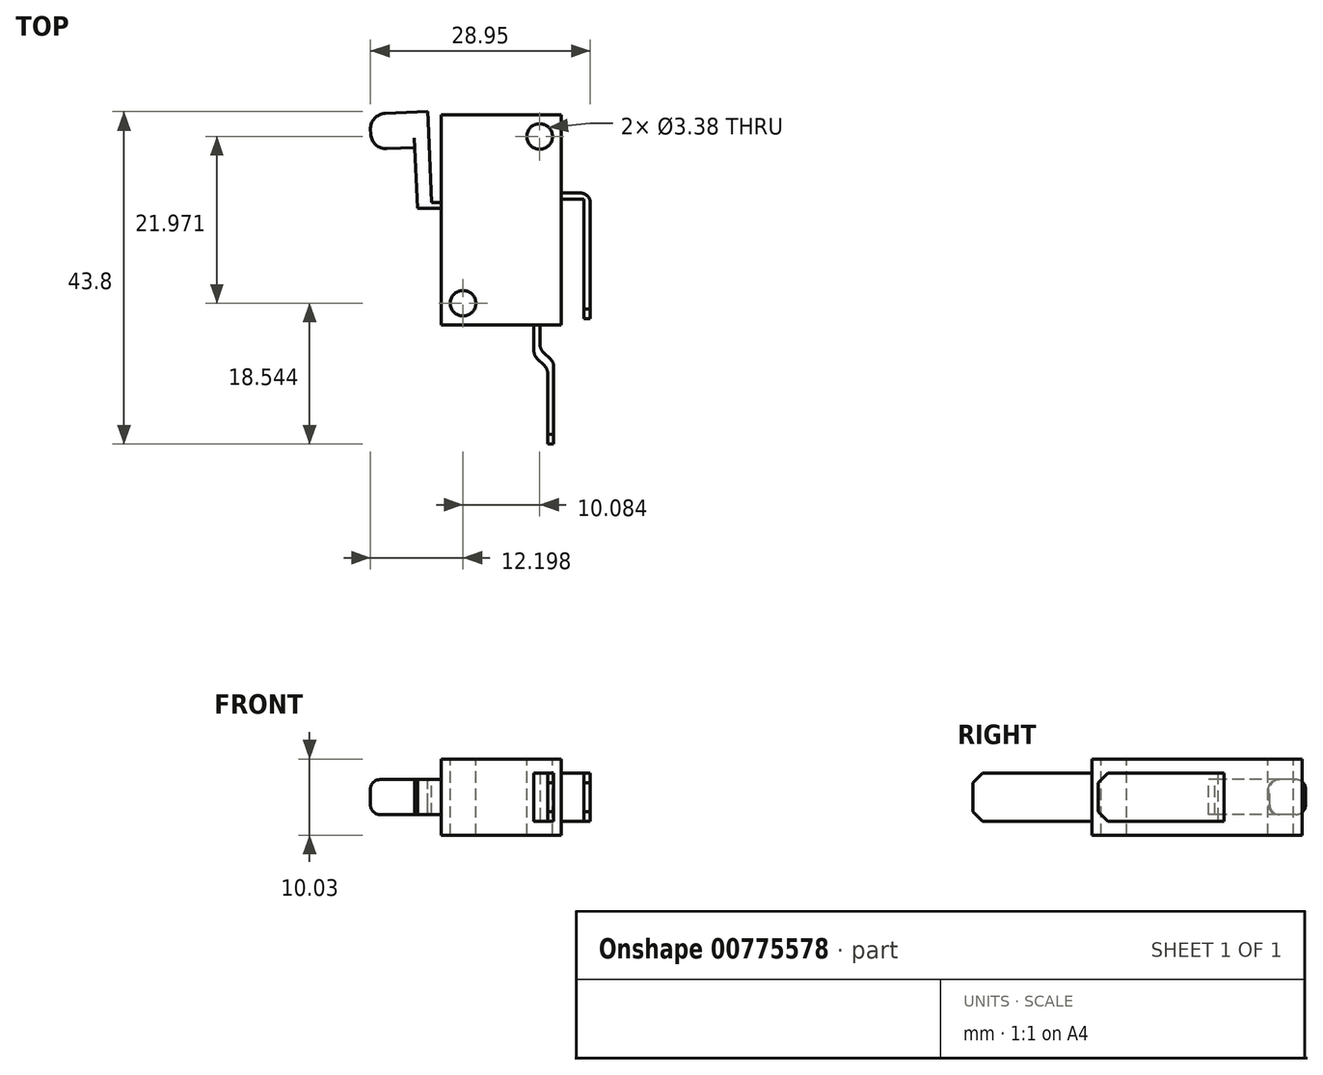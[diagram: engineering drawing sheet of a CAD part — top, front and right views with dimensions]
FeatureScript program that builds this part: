
annotation { "Feature Type Name" : "Feature", "Feature Type Description" : "" }
export const myFeature = defineFeature(function(context is Context, id is Id, definition is map)
    precondition{}
    {
        {
            var Q0;
            Q0=qCreatedBy(makeId("Top.planeOp"),FACE);
            var sketch = newSketch(context, id + "F0", { "sketchPlane" : qUnion([Q0])});
            skLineSegment(sketch, "E0.bottom", {"start": v(7.9, -13.84) * mm, "end": v(-7.9, -13.84) * mm});
            skLineSegment(sketch, "E0.top", {"start": v(7.9, 13.84) * mm, "end": v(-7.9, 13.84) * mm});
            skLineSegment(sketch, "E0.left", {"start": v(7.9, -13.84) * mm, "end": v(7.9, 13.84) * mm});
            skLineSegment(sketch, "E0.right", {"start": v(-7.9, -13.84) * mm, "end": v(-7.9, 13.84) * mm});
            skPoint(sketch, "E0.middle", {"position": v(0, 0) * mm});
            skSolve(sketch);
        }
        {
            var Q0;
            Q0 = qSketchRegion(id + "F0", true);
            extrude(context, id + "F1", {"entities" : qUnion([Q0]), "depth" : 10.03 * mm, "offsetDistance" : 25.4 * mm});
        }
        {
            var Q0;
            Q0=makeQuery(id+"F1.opExtrude","CAP_FACE",FACE,{"disambiguationData":[OSD([sQuery(id+"F0.wireOp",EDGE,"E0.bottom"),sQuery(id+"F0.wireOp",EDGE,"E0.top"),sQuery(id+"F0.wireOp",EDGE,"E0.left"),sQuery(id+"F0.wireOp",EDGE,"E0.right")])],"isStart":false});
            var sketch = newSketch(context, id + "F2", { "sketchPlane" : qUnion([Q0])});
            skCircle(sketch, "E1", {"center": v(5.04, 10.99) * mm, "radius": 1.69 * mm});
            skCircle(sketch, "E2", {"center": v(-5.04, -10.99) * mm, "radius": 1.69 * mm});
            skSolve(sketch);
        }
        {
            var Q0;
            Q0 = qSketchRegion(id + "F2", true);
            extrude(context, id + "F3", {"entities" : qUnion([Q0]), "operationType" : NewBodyOperationType.REMOVE, "endBound" : BoundingType.UP_TO_NEXT, "oppositeDirection" : true, "depth" : 25.4 * mm, "offsetDistance" : 25.4 * mm});
        }
        {
            var Q0;
            Q0=makeQuery(id+"F1.opExtrude","SWEPT_FACE",FACE,{"disambiguationData":[OSD([sQuery(id+"F0.wireOp",EDGE,"E0.left")])]});
            var sketch = newSketch(context, id + "F4", { "sketchPlane" : qUnion([Q0])});
            skLineSegment(sketch, "E3.bottom", {"start": v(3.53, 8.2) * mm, "end": v(2.72, 8.2) * mm});
            skLineSegment(sketch, "E3.top", {"start": v(3.53, 1.84) * mm, "end": v(2.72, 1.84) * mm});
            skLineSegment(sketch, "E3.left", {"start": v(3.53, 8.2) * mm, "end": v(3.53, 1.84) * mm});
            skLineSegment(sketch, "E3.right", {"start": v(2.72, 8.2) * mm, "end": v(2.72, 1.84) * mm});
            skLineSegment(sketch, "E4", {"start": v(13.84, 5.02) * mm, "end": v(-13.84, 5.02) * mm});
            skSolve(sketch);
        }
        {
            var Q0;
            Q0 = qSketchRegion(id + "F4", true);
            extrude(context, id + "F5", {"entities" : qUnion([Q0]), "operationType" : NewBodyOperationType.ADD, "depth" : 19.56 * mm - 15.75 * mm, "offsetDistance" : 25.4 * mm});
        }
        {
            var Q0;
            Q0=makeQuery(id+"F5.opExtrude","SWEPT_FACE",FACE,{"disambiguationData":[OSD([sQuery(id+"F4.wireOp",EDGE,"E3.right")])]});
            var sketch = newSketch(context, id + "F6", { "sketchPlane" : qUnion([Q0])});
            skLineSegment(sketch, "E5.bottom", {"start": v(11.7, 8.2) * mm, "end": v(10.9, 8.2) * mm});
            skLineSegment(sketch, "E5.top", {"start": v(11.7, 1.84) * mm, "end": v(10.9, 1.84) * mm});
            skLineSegment(sketch, "E5.left", {"start": v(11.7, 8.2) * mm, "end": v(11.7, 1.84) * mm});
            skLineSegment(sketch, "E5.right", {"start": v(10.9, 8.2) * mm, "end": v(10.9, 1.84) * mm});
            skSolve(sketch);
        }
        {
            var Q0;
            Q0 = qSketchRegion(id + "F6", true);
            extrude(context, id + "F7", {"entities" : qUnion([Q0]), "operationType" : NewBodyOperationType.ADD, "depth" : 15.75 * mm, "offsetDistance" : 25.4 * mm});
        }
        {
            var Q0;
            Q0=makeQuery(id+"F5.opExtrude","CAP_EDGE",EDGE,{"disambiguationData":[OSD([sQuery(id+"F4.wireOp",EDGE,"E3.left")])],"isStart":false});
            var Q1;
            Q1=makeQuery(id+"F7.opExtrude","CAP_EDGE",EDGE,{"disambiguationData":[OSD([sQuery(id+"F6.wireOp",EDGE,"E5.right")])],"isStart":true});
            fillet(context, id + "F8", {"entities" : qUnion([Q0, Q1]), "radius" : 1.27 * mm, "tangentPropagation" : true, "allowEdgeOverflow" : false});
        }
        {
            var Q0;
            Q0=makeQuery(id+"F7.opExtrude","CAP_EDGE",EDGE,{"disambiguationData":[OSD([sQuery(id+"F6.wireOp",EDGE,"E5.bottom")])],"isStart":false});
            var Q1;
            Q1=makeQuery(id+"F7.opExtrude","CAP_EDGE",EDGE,{"disambiguationData":[OSD([sQuery(id+"F6.wireOp",EDGE,"E5.top")])],"isStart":false});
            chamfer(context, id + "F9", {"entities" : qUnion([Q0, Q1]), "width" : 1.27 * mm, "tangentPropagation" : true});
        }
        {
            var Q0;
            Q0=makeQuery(id+"F1.opExtrude","SWEPT_FACE",FACE,{"disambiguationData":[OSD([sQuery(id+"F0.wireOp",EDGE,"E0.bottom")])]});
            var sketch = newSketch(context, id + "F10", { "sketchPlane" : qUnion([Q0])});
            skLineSegment(sketch, "E6.bottom", {"start": v(5.1, 8.2) * mm, "end": v(4.3, 8.2) * mm});
            skLineSegment(sketch, "E6.top", {"start": v(5.1, 1.84) * mm, "end": v(4.3, 1.84) * mm});
            skLineSegment(sketch, "E6.left", {"start": v(5.1, 8.2) * mm, "end": v(5.1, 1.84) * mm});
            skLineSegment(sketch, "E6.right", {"start": v(4.3, 8.2) * mm, "end": v(4.3, 1.84) * mm});
            skLineSegment(sketch, "E7", {"start": v(7.9, 5.02) * mm, "end": v(-7.9, 5.02) * mm});
            skSolve(sketch);
        }
        {
            var Q0;
            Q0 = qSketchRegion(id + "F10", true);
            extrude(context, id + "F11", {"entities" : qUnion([Q0]), "operationType" : NewBodyOperationType.ADD, "depth" : 3.17 * mm, "offsetDistance" : 25.4 * mm});
        }
        {
            var Q0;
            Q0=makeQuery(id+"F11.opExtrude","SWEPT_FACE",FACE,{"disambiguationData":[OSD([sQuery(id+"F10.wireOp",EDGE,"E6.bottom")])]});
            var sketch = newSketch(context, id + "F12", { "sketchPlane" : qUnion([Q0])});
            skLineSegment(sketch, "E8", {"start": v(5.1, -17.02) * mm, "end": v(4.3, -17.02) * mm});
            skLineSegment(sketch, "E9", {"start": v(4.3, -17.02) * mm, "end": v(4.3, -17.83) * mm});
            skLineSegment(sketch, "E10", {"start": v(4.3, -17.83) * mm, "end": v(5.1, -17.02) * mm});
            skSolve(sketch);
        }
        {
            var Q0;
            Q0 = qSketchRegion(id + "F12", true);
            var Q1;
            Q1=makeQuery(id+"F11.opExtrude","SWEPT_FACE",FACE,{"disambiguationData":[OSD([sQuery(id+"F10.wireOp",EDGE,"E6.top")])]});
            extrude(context, id + "F13", {"entities" : qUnion([Q0]), "operationType" : NewBodyOperationType.ADD, "endBound" : BoundingType.UP_TO_SURFACE, "oppositeDirection" : true, "depth" : 25.4 * mm, "endBoundEntityFace" : qUnion([Q1]), "offsetDistance" : 25.4 * mm});
        }
        {
            var Q0;
            Q0=makeQuery(id+"F13.opExtrude","SWEPT_FACE",FACE,{"disambiguationData":[OSD([sQuery(id+"F12.wireOp",EDGE,"E10")])]});
            var sketch = newSketch(context, id + "F14", { "sketchPlane" : qUnion([Q0])});
            skLineSegment(sketch, "E11.bottom", {"start": v(-8.42, 8.2) * mm, "end": v(-9.57, 8.2) * mm});
            skLineSegment(sketch, "E11.top", {"start": v(-8.42, 1.84) * mm, "end": v(-9.57, 1.84) * mm});
            skLineSegment(sketch, "E11.left", {"start": v(-8.42, 8.2) * mm, "end": v(-8.42, 1.84) * mm});
            skLineSegment(sketch, "E11.right", {"start": v(-9.57, 8.2) * mm, "end": v(-9.57, 1.84) * mm});
            skSolve(sketch);
        }
        {
            var Q0;
            Q0 = qSketchRegion(id + "F14", true);
            extrude(context, id + "F15", {"entities" : qUnion([Q0]), "operationType" : NewBodyOperationType.ADD, "depth" : 2.54 * mm, "offsetDistance" : 25.4 * mm});
        }
        {
            var Q0;
            Q0=makeQuery(id+"F15.boolean.opBoolean","MERGE",FACE,{"derivedFrom":[makeQuery(id+"F13.boolean.opBoolean","MERGE",FACE,{"derivedFrom":[makeQuery(id+"F11.opExtrude","SWEPT_FACE",FACE,{"disambiguationData":[OSD([sQuery(id+"F10.wireOp",EDGE,"E6.bottom")])]}),makeQuery(id+"F13.opExtrude","CAP_FACE",FACE,{"disambiguationData":[OSD([sQuery(id+"F12.wireOp",EDGE,"E8"),sQuery(id+"F12.wireOp",EDGE,"E9"),sQuery(id+"F12.wireOp",EDGE,"E10")])],"isStart":true})]}),makeQuery(id+"F15.opExtrude","SWEPT_FACE",FACE,{"disambiguationData":[OSD([sQuery(id+"F14.wireOp",EDGE,"E11.bottom")])]})]});
            var sketch = newSketch(context, id + "F16", { "sketchPlane" : qUnion([Q0])});
            skLineSegment(sketch, "E12", {"start": v(6.9, -18.81) * mm, "end": v(6.9, -19.63) * mm});
            skLineSegment(sketch, "E13", {"start": v(6.9, -19.63) * mm, "end": v(6.09, -19.63) * mm});
            skLineSegment(sketch, "E14", {"start": v(6.09, -19.63) * mm, "end": v(6.9, -18.81) * mm});
            skSolve(sketch);
        }
        {
            var Q0;
            Q0 = qSketchRegion(id + "F16", true);
            var Q1;
            {var subQ0=sQuery(id+"F10.wireOp",EDGE,"E6.top");Q1=makeQuery(id+"F15.boolean.opBoolean","MERGE",FACE,{"derivedFrom":[makeQuery(id+"F13.boolean.opBoolean","MERGE",FACE,{"derivedFrom":[makeQuery(id+"F11.opExtrude","SWEPT_FACE",FACE,{"disambiguationData":[OSD([subQ0])]}),makeQuery(id+"F13.opExtrude","CAP_FACE",FACE,{"disambiguationData":[OSD([subQ0])],"isStart":false})]}),makeQuery(id+"F15.opExtrude","SWEPT_FACE",FACE,{"disambiguationData":[OSD([sQuery(id+"F14.wireOp",EDGE,"E11.top")])]})]});}
            extrude(context, id + "F17", {"entities" : qUnion([Q0]), "operationType" : NewBodyOperationType.ADD, "endBound" : BoundingType.UP_TO_SURFACE, "oppositeDirection" : true, "depth" : 25.4 * mm, "endBoundEntityFace" : qUnion([Q1]), "offsetDistance" : 25.4 * mm});
        }
        {
            var Q0;
            Q0=makeQuery(id+"F17.opExtrude","SWEPT_FACE",FACE,{"disambiguationData":[OSD([sQuery(id+"F16.wireOp",EDGE,"E13")])]});
            var sketch = newSketch(context, id + "F18", { "sketchPlane" : qUnion([Q0])});
            skLineSegment(sketch, "E15.bottom", {"start": v(6.09, 8.2) * mm, "end": v(6.9, 8.2) * mm});
            skLineSegment(sketch, "E15.top", {"start": v(6.09, 1.84) * mm, "end": v(6.9, 1.84) * mm});
            skLineSegment(sketch, "E15.left", {"start": v(6.09, 8.2) * mm, "end": v(6.09, 1.84) * mm});
            skLineSegment(sketch, "E15.right", {"start": v(6.9, 8.2) * mm, "end": v(6.9, 1.84) * mm});
            skSolve(sketch);
        }
        {
            var Q0;
            Q0 = qSketchRegion(id + "F18", true);
            extrude(context, id + "F19", {"entities" : qUnion([Q0]), "operationType" : NewBodyOperationType.ADD, "depth" : 9.9 * mm, "offsetDistance" : 25.4 * mm});
        }
        {
            var Q0;
            Q0=makeQuery(id+"F15.boolean.opBoolean","MERGE",EDGE,{"derivedFrom":[makeQuery(id+"F13.opExtrude","SWEPT_EDGE",EDGE,{"disambiguationData":[OSD([sQuery(id+"F12.wireOp",EDGE,"E9"),sQuery(id+"F12.wireOp",EDGE,"E10")])]}),makeQuery(id+"F15.opExtrude","CAP_EDGE",EDGE,{"disambiguationData":[OSD([sQuery(id+"F14.wireOp",EDGE,"E11.right")])],"isStart":true})]});
            var Q1;
            {var subQ0=sQuery(id+"F10.wireOp",EDGE,"E6.left");Q1=makeQuery(id+"F15.boolean.opBoolean","MERGE",EDGE,{"derivedFrom":[makeQuery(id+"F13.boolean.opBoolean","MERGE",EDGE,{"derivedFrom":[makeQuery(id+"F11.opExtrude","CAP_EDGE",EDGE,{"disambiguationData":[OSD([subQ0])],"isStart":false}),makeQuery(id+"F13.opExtrude","SWEPT_EDGE",EDGE,{"disambiguationData":[OSD([sQuery(id+"F10.wireOp",EDGE,"E6.bottom"),subQ0,sQuery(id+"F12.wireOp",EDGE,"E8"),sQuery(id+"F12.wireOp",EDGE,"E10")])]})]}),makeQuery(id+"F15.opExtrude","CAP_EDGE",EDGE,{"disambiguationData":[OSD([sQuery(id+"F14.wireOp",EDGE,"E11.left")])],"isStart":true})]});}
            var Q2;
            {var subQ0=sQuery(id+"F14.wireOp",EDGE,"E11.left");Q2=makeQuery(id+"F17.boolean.opBoolean","MERGE",EDGE,{"derivedFrom":[makeQuery(id+"F15.opExtrude","CAP_EDGE",EDGE,{"disambiguationData":[OSD([subQ0])],"isStart":false}),makeQuery(id+"F17.opExtrude","SWEPT_EDGE",EDGE,{"disambiguationData":[OSD([sQuery(id+"F14.wireOp",EDGE,"E11.bottom"),subQ0,sQuery(id+"F16.wireOp",EDGE,"E12"),sQuery(id+"F16.wireOp",EDGE,"E14")])]})]});}
            var Q3;
            {var subQ0=sQuery(id+"F14.wireOp",EDGE,"E11.right");Q3=makeQuery(id+"F19.boolean.opBoolean","MERGE",EDGE,{"derivedFrom":[makeQuery(id+"F17.boolean.opBoolean","MERGE",EDGE,{"derivedFrom":[makeQuery(id+"F15.opExtrude","CAP_EDGE",EDGE,{"disambiguationData":[OSD([subQ0])],"isStart":false}),makeQuery(id+"F17.opExtrude","SWEPT_EDGE",EDGE,{"disambiguationData":[OSD([sQuery(id+"F14.wireOp",EDGE,"E11.bottom"),subQ0,sQuery(id+"F16.wireOp",EDGE,"E13"),sQuery(id+"F16.wireOp",EDGE,"E14")])]})]}),makeQuery(id+"F19.opExtrude","CAP_EDGE",EDGE,{"disambiguationData":[OSD([sQuery(id+"F18.wireOp",EDGE,"E15.left")])],"isStart":true})]});}
            fillet(context, id + "F20", {"entities" : qUnion([Q0, Q1, Q2, Q3]), "radius" : 1.27 * mm, "tangentPropagation" : true, "allowEdgeOverflow" : false});
        }
        {
            var Q0;
            Q0=makeQuery(id+"F19.opExtrude","CAP_EDGE",EDGE,{"disambiguationData":[OSD([sQuery(id+"F18.wireOp",EDGE,"E15.top")])],"isStart":false});
            var Q1;
            Q1=makeQuery(id+"F19.opExtrude","CAP_EDGE",EDGE,{"disambiguationData":[OSD([sQuery(id+"F18.wireOp",EDGE,"E15.bottom")])],"isStart":false});
            chamfer(context, id + "F21", {"entities" : qUnion([Q0, Q1]), "width" : 1.27 * mm, "tangentPropagation" : true});
        }
        {
            var Q0;
            Q0=makeQuery(id+"F1.opExtrude","SWEPT_FACE",FACE,{"disambiguationData":[OSD([sQuery(id+"F0.wireOp",EDGE,"E0.right")])]});
            var sketch = newSketch(context, id + "F22", { "sketchPlane" : qUnion([Q0])});
            skLineSegment(sketch, "E16.bottom", {"start": v(-2.31, 2.72) * mm, "end": v(-1.5, 2.72) * mm});
            skLineSegment(sketch, "E16.top", {"start": v(-2.31, 7.32) * mm, "end": v(-1.5, 7.32) * mm});
            skLineSegment(sketch, "E16.left", {"start": v(-2.31, 2.72) * mm, "end": v(-2.31, 7.32) * mm});
            skLineSegment(sketch, "E16.right", {"start": v(-1.5, 2.72) * mm, "end": v(-1.5, 7.32) * mm});
            skLineSegment(sketch, "E17", {"start": v(-13.84, 5.02) * mm, "end": v(13.84, 5.02) * mm});
            skSolve(sketch);
        }
        {
            var Q0;
            Q0 = qSketchRegion(id + "F22", true);
            extrude(context, id + "F23", {"entities" : qUnion([Q0]), "operationType" : NewBodyOperationType.ADD, "depth" : 1.27 * mm, "offsetDistance" : 25.4 * mm});
        }
        {
            var Q0;
            Q0=makeQuery(id+"F23.opExtrude","SWEPT_FACE",FACE,{"disambiguationData":[OSD([sQuery(id+"F22.wireOp",EDGE,"E16.top")])]});
            var sketch = newSketch(context, id + "F24", { "sketchPlane" : qUnion([Q0])});
            skLineSegment(sketch, "E18", {"start": v(-9.17, 1.58) * mm, "end": v(-9.17, 1.5) * mm});
            skLineSegment(sketch, "E19", {"start": v(-9.17, 1.5) * mm, "end": v(-11.06, 1.5) * mm});
            skLineSegment(sketch, "E20", {"start": v(-11.06, 1.5) * mm, "end": v(-9.17, 1.58) * mm});
            skSolve(sketch);
        }
        {
            var Q0;
            Q0 = qSketchRegion(id + "F24", true);
            var Q1;
            Q1=makeQuery(id+"F23.opExtrude","SWEPT_FACE",FACE,{"disambiguationData":[OSD([sQuery(id+"F22.wireOp",EDGE,"E16.bottom")])]});
            extrude(context, id + "F25", {"entities" : qUnion([Q0]), "operationType" : NewBodyOperationType.ADD, "endBound" : BoundingType.UP_TO_SURFACE, "oppositeDirection" : true, "depth" : 25.4 * mm, "endBoundEntityFace" : qUnion([Q1]), "offsetDistance" : 25.4 * mm});
        }
        {
            var Q0;
            Q0=makeQuery(id+"F25.opExtrude","SWEPT_FACE",FACE,{"disambiguationData":[OSD([sQuery(id+"F24.wireOp",EDGE,"E20")])]});
            var sketch = newSketch(context, id + "F26", { "sketchPlane" : qUnion([Q0])});
            skLineSegment(sketch, "E21.bottom", {"start": v(10.99, 2.72) * mm, "end": v(9.06, 2.72) * mm});
            skLineSegment(sketch, "E21.top", {"start": v(10.99, 7.32) * mm, "end": v(9.06, 7.32) * mm});
            skLineSegment(sketch, "E21.left", {"start": v(10.99, 2.72) * mm, "end": v(10.99, 7.32) * mm});
            skLineSegment(sketch, "E21.right", {"start": v(9.06, 2.72) * mm, "end": v(9.06, 7.32) * mm});
            skSolve(sketch);
        }
        {
            var Q0;
            Q0 = qSketchRegion(id + "F26", true);
            extrude(context, id + "F27", {"entities" : qUnion([Q0]), "operationType" : NewBodyOperationType.ADD, "depth" : 12.7 * mm, "offsetDistance" : 25.4 * mm});
        }
        {
            var Q0;
            Q0=makeQuery(id+"F27.opExtrude","SWEPT_FACE",FACE,{"disambiguationData":[OSD([sQuery(id+"F26.wireOp",EDGE,"E21.left")])]});
            var sketch = newSketch(context, id + "F28", { "sketchPlane" : qUnion([Q0])});
            skLineSegment(sketch, "E22.bottom", {"start": v(-14.68, 2.72) * mm, "end": v(-10.03, 2.72) * mm});
            skLineSegment(sketch, "E22.top", {"start": v(-14.68, 7.32) * mm, "end": v(-10.03, 7.32) * mm});
            skLineSegment(sketch, "E22.left", {"start": v(-14.68, 2.72) * mm, "end": v(-14.68, 7.32) * mm});
            skLineSegment(sketch, "E22.right", {"start": v(-10.03, 2.72) * mm, "end": v(-10.03, 7.32) * mm});
            skSolve(sketch);
        }
        {
            var Q0;
            Q0 = qSketchRegion(id + "F28", true);
            extrude(context, id + "F29", {"entities" : qUnion([Q0]), "operationType" : NewBodyOperationType.ADD, "depth" : 5.7 * mm, "offsetDistance" : 25.4 * mm});
        }
        {
            var Q0;
            Q0=makeQuery(id+"F29.opExtrude","CAP_EDGE",EDGE,{"disambiguationData":[OSD([sQuery(id+"F28.wireOp",EDGE,"E22.right")])],"isStart":false});
            var Q1;
            Q1=makeQuery(id+"F29.opExtrude","CAP_EDGE",EDGE,{"disambiguationData":[OSD([sQuery(id+"F28.wireOp",EDGE,"E22.left")])],"isStart":false});
            fillet(context, id + "F30", {"entities" : qUnion([Q0, Q1]), "radius" : 2.03 * mm, "tangentPropagation" : true, "allowEdgeOverflow" : false});
        }
        {
            var Q0;
            Q0=makeQuery(id+"F30.opFillet","BLEND_EDGE",EDGE,{"blendedFrom":[makeQuery(id+"F29.opExtrude","CAP_EDGE",EDGE,{"disambiguationData":[OSD([sQuery(id+"F28.wireOp",EDGE,"E22.left")])],"isStart":false}),makeQuery(id+"F29.boolean.opBoolean","MERGE",FACE,{"derivedFrom":[makeQuery(id+"F27.boolean.opBoolean","MERGE",FACE,{"derivedFrom":[makeQuery(id+"F25.boolean.opBoolean","MERGE",FACE,{"derivedFrom":[makeQuery(id+"F23.opExtrude","SWEPT_FACE",FACE,{"disambiguationData":[OSD([sQuery(id+"F22.wireOp",EDGE,"E16.top")])]}),makeQuery(id+"F25.opExtrude","CAP_FACE",FACE,{"disambiguationData":[OSD([sQuery(id+"F24.wireOp",EDGE,"E18"),sQuery(id+"F24.wireOp",EDGE,"E19"),sQuery(id+"F24.wireOp",EDGE,"E20")])],"isStart":true})]}),makeQuery(id+"F27.opExtrude","SWEPT_FACE",FACE,{"disambiguationData":[OSD([sQuery(id+"F26.wireOp",EDGE,"E21.top")])]})]}),makeQuery(id+"F29.opExtrude","SWEPT_FACE",FACE,{"disambiguationData":[OSD([sQuery(id+"F28.wireOp",EDGE,"E22.top")])]})]})],"blendedInto":[makeQuery(id+"F29.boolean.opBoolean","MERGE",FACE,{"derivedFrom":[makeQuery(id+"F27.boolean.opBoolean","MERGE",FACE,{"derivedFrom":[makeQuery(id+"F25.boolean.opBoolean","MERGE",FACE,{"derivedFrom":[makeQuery(id+"F23.opExtrude","SWEPT_FACE",FACE,{"disambiguationData":[OSD([sQuery(id+"F22.wireOp",EDGE,"E16.top")])]}),makeQuery(id+"F25.opExtrude","CAP_FACE",FACE,{"disambiguationData":[OSD([sQuery(id+"F24.wireOp",EDGE,"E18"),sQuery(id+"F24.wireOp",EDGE,"E19"),sQuery(id+"F24.wireOp",EDGE,"E20")])],"isStart":true})]}),makeQuery(id+"F27.opExtrude","SWEPT_FACE",FACE,{"disambiguationData":[OSD([sQuery(id+"F26.wireOp",EDGE,"E21.top")])]})]}),makeQuery(id+"F29.opExtrude","SWEPT_FACE",FACE,{"disambiguationData":[OSD([sQuery(id+"F28.wireOp",EDGE,"E22.top")])]})]})]});
            var Q1;
            Q1=makeQuery(id+"F30.opFillet","BLEND_EDGE",EDGE,{"blendedFrom":[makeQuery(id+"F29.opExtrude","CAP_EDGE",EDGE,{"disambiguationData":[OSD([sQuery(id+"F28.wireOp",EDGE,"E22.right")])],"isStart":false}),makeQuery(id+"F29.boolean.opBoolean","MERGE",FACE,{"derivedFrom":[makeQuery(id+"F27.boolean.opBoolean","MERGE",FACE,{"derivedFrom":[makeQuery(id+"F25.boolean.opBoolean","MERGE",FACE,{"derivedFrom":[makeQuery(id+"F23.opExtrude","SWEPT_FACE",FACE,{"disambiguationData":[OSD([sQuery(id+"F22.wireOp",EDGE,"E16.top")])]}),makeQuery(id+"F25.opExtrude","CAP_FACE",FACE,{"disambiguationData":[OSD([sQuery(id+"F24.wireOp",EDGE,"E18"),sQuery(id+"F24.wireOp",EDGE,"E19"),sQuery(id+"F24.wireOp",EDGE,"E20")])],"isStart":true})]}),makeQuery(id+"F27.opExtrude","SWEPT_FACE",FACE,{"disambiguationData":[OSD([sQuery(id+"F26.wireOp",EDGE,"E21.top")])]})]}),makeQuery(id+"F29.opExtrude","SWEPT_FACE",FACE,{"disambiguationData":[OSD([sQuery(id+"F28.wireOp",EDGE,"E22.top")])]})]})],"blendedInto":[makeQuery(id+"F29.boolean.opBoolean","MERGE",FACE,{"derivedFrom":[makeQuery(id+"F27.boolean.opBoolean","MERGE",FACE,{"derivedFrom":[makeQuery(id+"F25.boolean.opBoolean","MERGE",FACE,{"derivedFrom":[makeQuery(id+"F23.opExtrude","SWEPT_FACE",FACE,{"disambiguationData":[OSD([sQuery(id+"F22.wireOp",EDGE,"E16.top")])]}),makeQuery(id+"F25.opExtrude","CAP_FACE",FACE,{"disambiguationData":[OSD([sQuery(id+"F24.wireOp",EDGE,"E18"),sQuery(id+"F24.wireOp",EDGE,"E19"),sQuery(id+"F24.wireOp",EDGE,"E20")])],"isStart":true})]}),makeQuery(id+"F27.opExtrude","SWEPT_FACE",FACE,{"disambiguationData":[OSD([sQuery(id+"F26.wireOp",EDGE,"E21.top")])]})]}),makeQuery(id+"F29.opExtrude","SWEPT_FACE",FACE,{"disambiguationData":[OSD([sQuery(id+"F28.wireOp",EDGE,"E22.top")])]})]})]});
            var Q2;
            Q2=makeQuery(id+"F29.opExtrude","CAP_EDGE",EDGE,{"disambiguationData":[OSD([sQuery(id+"F28.wireOp",EDGE,"E22.top")])],"isStart":false});
            var Q3;
            Q3=makeQuery(id+"F29.opExtrude","CAP_EDGE",EDGE,{"disambiguationData":[OSD([sQuery(id+"F28.wireOp",EDGE,"E22.bottom")])],"isStart":false});
            var Q4;
            {var subQ0=sQuery(id+"F22.wireOp",EDGE,"E16.bottom");Q4=makeQuery(id+"F30.opFillet","BLEND_EDGE",EDGE,{"blendedFrom":[makeQuery(id+"F29.opExtrude","CAP_EDGE",EDGE,{"disambiguationData":[OSD([sQuery(id+"F28.wireOp",EDGE,"E22.right")])],"isStart":false}),makeQuery(id+"F29.boolean.opBoolean","MERGE",FACE,{"derivedFrom":[makeQuery(id+"F27.boolean.opBoolean","MERGE",FACE,{"derivedFrom":[makeQuery(id+"F25.boolean.opBoolean","MERGE",FACE,{"derivedFrom":[makeQuery(id+"F23.opExtrude","SWEPT_FACE",FACE,{"disambiguationData":[OSD([subQ0])]}),makeQuery(id+"F25.opExtrude","CAP_FACE",FACE,{"disambiguationData":[OSD([subQ0])],"isStart":false})]}),makeQuery(id+"F27.opExtrude","SWEPT_FACE",FACE,{"disambiguationData":[OSD([sQuery(id+"F26.wireOp",EDGE,"E21.bottom")])]})]}),makeQuery(id+"F29.opExtrude","SWEPT_FACE",FACE,{"disambiguationData":[OSD([sQuery(id+"F28.wireOp",EDGE,"E22.bottom")])]})]})],"blendedInto":[makeQuery(id+"F29.boolean.opBoolean","MERGE",FACE,{"derivedFrom":[makeQuery(id+"F27.boolean.opBoolean","MERGE",FACE,{"derivedFrom":[makeQuery(id+"F25.boolean.opBoolean","MERGE",FACE,{"derivedFrom":[makeQuery(id+"F23.opExtrude","SWEPT_FACE",FACE,{"disambiguationData":[OSD([subQ0])]}),makeQuery(id+"F25.opExtrude","CAP_FACE",FACE,{"disambiguationData":[OSD([subQ0])],"isStart":false})]}),makeQuery(id+"F27.opExtrude","SWEPT_FACE",FACE,{"disambiguationData":[OSD([sQuery(id+"F26.wireOp",EDGE,"E21.bottom")])]})]}),makeQuery(id+"F29.opExtrude","SWEPT_FACE",FACE,{"disambiguationData":[OSD([sQuery(id+"F28.wireOp",EDGE,"E22.bottom")])]})]})]});}
            var Q5;
            {var subQ0=sQuery(id+"F22.wireOp",EDGE,"E16.bottom");Q5=makeQuery(id+"F30.opFillet","BLEND_EDGE",EDGE,{"blendedFrom":[makeQuery(id+"F29.opExtrude","CAP_EDGE",EDGE,{"disambiguationData":[OSD([sQuery(id+"F28.wireOp",EDGE,"E22.left")])],"isStart":false}),makeQuery(id+"F29.boolean.opBoolean","MERGE",FACE,{"derivedFrom":[makeQuery(id+"F27.boolean.opBoolean","MERGE",FACE,{"derivedFrom":[makeQuery(id+"F25.boolean.opBoolean","MERGE",FACE,{"derivedFrom":[makeQuery(id+"F23.opExtrude","SWEPT_FACE",FACE,{"disambiguationData":[OSD([subQ0])]}),makeQuery(id+"F25.opExtrude","CAP_FACE",FACE,{"disambiguationData":[OSD([subQ0])],"isStart":false})]}),makeQuery(id+"F27.opExtrude","SWEPT_FACE",FACE,{"disambiguationData":[OSD([sQuery(id+"F26.wireOp",EDGE,"E21.bottom")])]})]}),makeQuery(id+"F29.opExtrude","SWEPT_FACE",FACE,{"disambiguationData":[OSD([sQuery(id+"F28.wireOp",EDGE,"E22.bottom")])]})]})],"blendedInto":[makeQuery(id+"F29.boolean.opBoolean","MERGE",FACE,{"derivedFrom":[makeQuery(id+"F27.boolean.opBoolean","MERGE",FACE,{"derivedFrom":[makeQuery(id+"F25.boolean.opBoolean","MERGE",FACE,{"derivedFrom":[makeQuery(id+"F23.opExtrude","SWEPT_FACE",FACE,{"disambiguationData":[OSD([subQ0])]}),makeQuery(id+"F25.opExtrude","CAP_FACE",FACE,{"disambiguationData":[OSD([subQ0])],"isStart":false})]}),makeQuery(id+"F27.opExtrude","SWEPT_FACE",FACE,{"disambiguationData":[OSD([sQuery(id+"F26.wireOp",EDGE,"E21.bottom")])]})]}),makeQuery(id+"F29.opExtrude","SWEPT_FACE",FACE,{"disambiguationData":[OSD([sQuery(id+"F28.wireOp",EDGE,"E22.bottom")])]})]})]});}
            fillet(context, id + "F31", {"entities" : qUnion([Q0, Q1, Q2, Q3, Q4, Q5]), "radius" : 1.27 * mm, "tangentPropagation" : true, "allowEdgeOverflow" : false});
        }
    });
